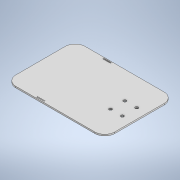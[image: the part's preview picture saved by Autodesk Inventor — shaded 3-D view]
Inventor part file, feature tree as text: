
AUTODESK INVENTOR PART (.ipt)
format: ipt  version: 2020 (Build 240168000, 168)  size: 141,312 bytes
history: native  units: mm
features: extrude x3, sketch x3, other x1, fillet x1
ambient origin geometry x8: Origin, YZ Plane, XZ Plane, XY Plane, X Axis, Y Axis, Z Axis, Center Point
bodies: Body1 (feature_tree)
feature tree (8):
  other  "Bryła1"
  extrude  "Wyciągnięcie proste1"  Depth=200.0mm
  extrude  "Wyciągnięcie proste2"  Depth=140.0mm
  extrude  "Wyciągnięcie proste3"  Depth=3.0mm TaperAngle=0.0deg
  fillet  "Zaokrąglenie1"  Radius=50.0mm
  sketch  "Szkic1"
  sketch  "Szkic2"
  sketch  "Szkic3"
